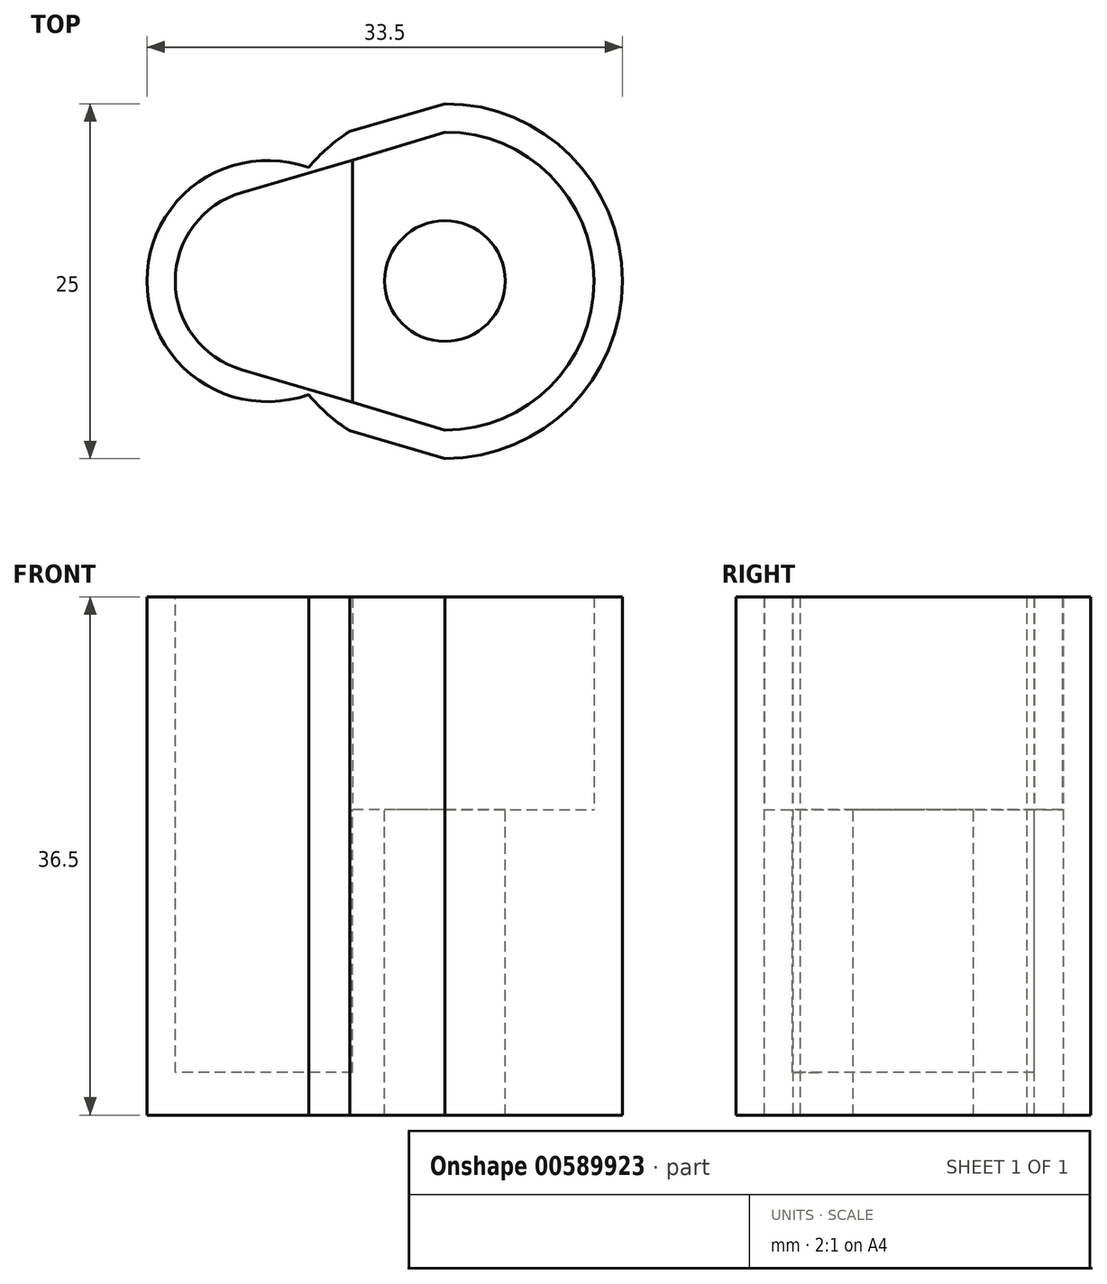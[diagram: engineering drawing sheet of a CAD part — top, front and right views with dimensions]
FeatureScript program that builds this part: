
annotation { "Feature Type Name" : "Feature", "Feature Type Description" : "" }
export const myFeature = defineFeature(function(context is Context, id is Id, definition is map)
    precondition{}
    {
        {
            var Q0;
            Q0=qCreatedBy(makeId("Top.planeOp"),FACE);
            var sketch = newSketch(context, id + "F0", { "sketchPlane" : qUnion([Q0])});
            skCircle(sketch, "E0", {"center": v(0, 0) * mm, "radius": 4 * mm});
            skCircle(sketch, "E1", {"center": v(0, 0) * mm, "radius": 12.5 * mm});
            skCircle(sketch, "E2", {"center": v(-12.5, 0) * mm, "radius": 8.5 * mm});
            skLineSegment(sketch, "E3", {"start": v(0, -12.5) * mm, "end": v(-14.88, -8.16) * mm});
            skLineSegment(sketch, "E4", {"start": v(0, 12.5) * mm, "end": v(-14.88, 8.16) * mm});
            skSolve(sketch);
        }
        {
            var Q0;
            {var subQ10=sQuery(id+"F0.wireOp",EDGE,"E0");Q0=makeQuery(id+"F0.imprint","IMPRINT",FACE,{"disambiguationData":[TD([[makeQuery(id+"F0.imprint","IMPRINT",EDGE,{"derivedFrom":subQ10}),-1.0]])]});}
            var Q1;
            {var subQ0=sQuery(id+"F0.wireOp",EDGE,"E3");var subQ1=sQuery(id+"F0.wireOp",EDGE,"E1");var subQ2=makeQuery(id+"F0.imprint","INTERSECT",VERTEX,{"disambiguationData":[OD(1.0)],"derivedFrom":[subQ1,subQ0]});Q1=makeQuery(id+"F0.imprint","IMPRINT",FACE,{"disambiguationData":[TD([[makeQuery(id+"F0.imprint","IMPRINT",EDGE,{"disambiguationData":[TD([[subQ2,1.0]])],"derivedFrom":subQ1}),-1.0]])]});}
            var Q2;
            {var subQ0=sQuery(id+"F0.wireOp",EDGE,"E2");var subQ1=sQuery(id+"F0.wireOp",EDGE,"E1");var subQ2=makeQuery(id+"F0.imprint","INTERSECT",VERTEX,{"disambiguationData":[OD(0.0)],"derivedFrom":[subQ1,subQ0]});Q2=makeQuery(id+"F0.imprint","IMPRINT",FACE,{"disambiguationData":[TD([[makeQuery(id+"F0.imprint","IMPRINT",EDGE,{"disambiguationData":[TD([[subQ2,-1.0]])],"derivedFrom":subQ1}),-1.0]])]});}
            var Q3;
            {var subQ0=sQuery(id+"F0.wireOp",EDGE,"E2");var subQ1=sQuery(id+"F0.wireOp",EDGE,"E1");var subQ2=makeQuery(id+"F0.imprint","INTERSECT",VERTEX,{"disambiguationData":[OD(0.0)],"derivedFrom":[subQ1,subQ0]});Q3=makeQuery(id+"F0.imprint","IMPRINT",FACE,{"disambiguationData":[TD([[makeQuery(id+"F0.imprint","IMPRINT",EDGE,{"disambiguationData":[TD([[subQ2,-1.0]])],"derivedFrom":subQ1}),1.0]])]});}
            var Q4;
            {var subQ0=sQuery(id+"F0.wireOp",EDGE,"E4");var subQ1=sQuery(id+"F0.wireOp",EDGE,"E1");var subQ2=makeQuery(id+"F0.imprint","INTERSECT",VERTEX,{"disambiguationData":[OD(1.0)],"derivedFrom":[subQ1,subQ0]});Q4=makeQuery(id+"F0.imprint","IMPRINT",FACE,{"disambiguationData":[TD([[makeQuery(id+"F0.imprint","IMPRINT",EDGE,{"disambiguationData":[TD([[subQ2,-1.0]])],"derivedFrom":subQ1}),-1.0]])]});}
            extrude(context, id + "F1", {"entities" : qUnion([Q0, Q1, Q2, Q3, Q4]), "depth" : 30 * mm, "offsetDistance" : 25 * mm});
        }
        {
            var Q0;
            Q0=makeQuery(id+"F1.opExtrude","CAP_FACE",FACE,{"disambiguationData":[OSD([sQuery(id+"F0.wireOp",EDGE,"E0"),sQuery(id+"F0.wireOp",EDGE,"E1"),sQuery(id+"F0.wireOp",EDGE,"E2"),sQuery(id+"F0.wireOp",EDGE,"E3"),sQuery(id+"F0.wireOp",EDGE,"E4")])],"isStart":false});
            var sketch = newSketch(context, id + "F2", { "sketchPlane" : qUnion([Q0])});
            skLineSegment(sketch, "E5.0", {"start": v(0.56, -10.58) * mm, "end": v(-14.32, -6.24) * mm});
            skArc(sketch, "E5.1", {"start": v(-14.32, 6.24) * mm, "mid": v(-19, 0) * mm, "end": v(-14.32, -6.24) * mm});
            skLineSegment(sketch, "E5.2", {"start": v(0.56, 10.58) * mm, "end": v(-14.32, 6.24) * mm});
            skLineSegment(sketch, "E6.bottom", {"start": v(6.5, 6.5) * mm, "end": v(-6.5, 6.5) * mm});
            skLineSegment(sketch, "E6.top", {"start": v(6.5, -6.5) * mm, "end": v(-6.5, -6.5) * mm});
            skLineSegment(sketch, "E6.right", {"start": v(-6.5, 6.5) * mm, "end": v(-6.5, -6.5) * mm});
            skPoint(sketch, "E6.middle", {"position": v(0, 0) * mm});
            skLineSegment(sketch, "E7", {"start": v(-6.5, -6.5) * mm, "end": v(-6.5, -8.52) * mm});
            skLineSegment(sketch, "E8", {"start": v(-6.5, 6.5) * mm, "end": v(-6.5, 8.52) * mm});
            skLineSegment(sketch, "E9", {"start": v(6.5, 0) * mm, "end": v(10, 0) * mm, "construction": true});
            skPoint(sketch, "E9.endSnap0", {"position": v(6.5, 0) * mm});
            skLineSegment(sketch, "E10", {"start": v(10, 0) * mm, "end": v(6.5, 6.5) * mm});
            skLineSegment(sketch, "E11", {"start": v(10, 0) * mm, "end": v(6.5, -6.5) * mm});
            skSolve(sketch);
        }
        {
            var Q0;
            {var subQ1=sQuery(id+"F2.wireOp",EDGE,"E5.1");Q0=makeQuery(id+"F2.imprint","IMPRINT",FACE,{"disambiguationData":[TD([[makeQuery(id+"F2.imprint","IMPRINT",EDGE,{"derivedFrom":subQ1}),1.0]])]});}
            extrude(context, id + "F3", {"entities" : qUnion([Q0]), "operationType" : NewBodyOperationType.REMOVE, "oppositeDirection" : true, "depth" : 27 * mm, "offsetDistance" : 25 * mm});
        }
        {
            var Q0;
            Q0=makeQuery(id+"F1.opExtrude","CAP_FACE",FACE,{"disambiguationData":[OSD([sQuery(id+"F0.wireOp",EDGE,"E0"),sQuery(id+"F0.wireOp",EDGE,"E1"),sQuery(id+"F0.wireOp",EDGE,"E2"),sQuery(id+"F0.wireOp",EDGE,"E3"),sQuery(id+"F0.wireOp",EDGE,"E4")])],"isStart":false});
            var sketch = newSketch(context, id + "F4", { "sketchPlane" : qUnion([Q0])});
            skCircle(sketch, "E12", {"center": v(0, 0) * mm, "radius": 4.25 * mm});
            skSolve(sketch);
        }
        {
            var Q0;
            Q0=makeQuery(id+"F2.imprint","IMPRINT",FACE,{"disambiguationData":[TD([[makeQuery(id+"F2.imprint","IMPRINT",EDGE,{"derivedFrom":sQuery(id+"F2.wireOp",EDGE,"E6.bottom")}),1.0]])]});
            extrude(context, id + "F5", {"entities" : qUnion([Q0]), "operationType" : NewBodyOperationType.REMOVE, "oppositeDirection" : true, "depth" : 6.5 * mm, "offsetDistance" : 25 * mm});
        }
        {
            var Q0;
            Q0=makeQuery(id+"F4.imprint","IMPRINT",FACE,{"disambiguationData":[TD([[makeQuery(id+"F4.imprint","IMPRINT",EDGE,{"derivedFrom":sQuery(id+"F4.wireOp",EDGE,"E12")}),1.0]])]});
            extrude(context, id + "F6", {"entities" : qUnion([Q0]), "operationType" : NewBodyOperationType.REMOVE, "oppositeDirection" : true, "depth" : 35.2 * mm, "offsetDistance" : 25 * mm});
        }
        {
            var Q0;
            Q0=makeQuery(id+"F1.opExtrude","CAP_FACE",FACE,{"disambiguationData":[OSD([sQuery(id+"F0.wireOp",EDGE,"E0"),sQuery(id+"F0.wireOp",EDGE,"E1"),sQuery(id+"F0.wireOp",EDGE,"E2"),sQuery(id+"F0.wireOp",EDGE,"E3"),sQuery(id+"F0.wireOp",EDGE,"E4")])],"isStart":false});
            extrude(context, id + "F7", {"entities" : qUnion([Q0]), "operationType" : NewBodyOperationType.ADD, "depth" : 10 * mm, "offsetDistance" : 25 * mm});
        }
        {
            var Q0;
            {var subQ0=sQuery(id+"F2.wireOp",EDGE,"E6.bottom");Q0=makeQuery(id+"F7.boolean.opBoolean","MERGE",FACE,{"derivedFrom":[makeQuery(id+"F5.boolean.opBoolean","COPY",FACE,{"derivedFrom":makeQuery(id+"F5.opExtrude","SWEPT_FACE",FACE,{"disambiguationData":[OSD([subQ0])]})}),makeQuery(id+"F7.opExtrude","SWEPT_FACE",FACE,{"disambiguationData":[OSD([subQ0])]})]});}
            var sketch = newSketch(context, id + "F8", { "sketchPlane" : qUnion([Q0])});
            skLineSegment(sketch, "E13.0", {"start": v(-5.5, 23.5) * mm, "end": v(-5.5, 40) * mm});
            skSolve(sketch);
        }
        {
            var Q0;
            {var subQ0=sQuery(id+"F8.wireOp",EDGE,"E13.0");Q0=makeQuery(id+"F8.imprint","IMPRINT",FACE,{"disambiguationData":[TD([[makeQuery(id+"F8.imprint","IMPRINT",EDGE,{"derivedFrom":subQ0}),1.0]])]});}
            extrude(context, id + "F9", {"entities" : qUnion([Q0]), "operationType" : NewBodyOperationType.ADD, "depth" : 13.4 * mm, "offsetDistance" : 25 * mm});
        }
        {
            var Q0;
            {var subQ2=sQuery(id+"F2.wireOp",EDGE,"E6.bottom");var subQ3=makeQuery(id+"F7.opExtrude","CAP_EDGE",EDGE,{"disambiguationData":[OSD([subQ2])],"isStart":false});Q0=makeQuery(id+"F9.boolean.opBoolean","MERGE",FACE,{"derivedFrom":[makeQuery(id+"F7.opExtrude","CAP_FACE",FACE,{"disambiguationData":[OSD([sQuery(id+"F0.wireOp",EDGE,"E0"),sQuery(id+"F0.wireOp",EDGE,"E1"),sQuery(id+"F0.wireOp",EDGE,"E2"),sQuery(id+"F0.wireOp",EDGE,"E3"),sQuery(id+"F0.wireOp",EDGE,"E4")])],"isStart":false}),makeQuery(id+"F9.opExtrude","SWEPT_FACE",FACE,{"disambiguationData":[OSD([subQ2]),TDD([makeQuery(id+"F8.imprint","IMPRINT",EDGE,{"disambiguationData":[TD([[makeQuery(id+"F8.imprint","INTERSECT",VERTEX,{"derivedFrom":[subQ3,sQuery(id+"F8.wireOp",EDGE,"E13.0")]}),-1.0]])],"derivedFrom":subQ3})])]})]});}
            var sketch = newSketch(context, id + "F10", { "sketchPlane" : qUnion([Q0])});
            skLineSegment(sketch, "E14", {"start": v(-5.5, -6.5) * mm, "end": v(0, -12.5) * mm});
            skLineSegment(sketch, "E15", {"start": v(-5.5, 6.5) * mm, "end": v(0, 12.5) * mm});
            skSolve(sketch);
        }
        {
            var Q0;
            Q0=makeQuery(id+"F10.imprint","IMPRINT",FACE,{"disambiguationData":[TD([[makeQuery(id+"F10.imprint","IMPRINT",EDGE,{"derivedFrom":sQuery(id+"F10.wireOp",EDGE,"E14")}),1.0]])]});
            extrude(context, id + "F11", {"entities" : qUnion([Q0]), "operationType" : NewBodyOperationType.REMOVE, "oppositeDirection" : true, "depth" : 16 * mm, "offsetDistance" : 25 * mm});
        }
        {
            var Q0;
            Q0=makeQuery(id+"F11.boolean.opBoolean","COPY",FACE,{"derivedFrom":makeQuery(id+"F11.opExtrude","CAP_FACE",FACE,{"disambiguationData":[OSD([sQuery(id+"F0.wireOp",EDGE,"E1"),sQuery(id+"F2.wireOp",EDGE,"E6.bottom"),sQuery(id+"F2.wireOp",EDGE,"E6.top"),sQuery(id+"F2.wireOp",EDGE,"E10"),sQuery(id+"F2.wireOp",EDGE,"E11"),sQuery(id+"F10.wireOp",EDGE,"E14"),sQuery(id+"F10.wireOp",EDGE,"E15")])],"isStart":false})});
            extrude(context, id + "F12", {"entities" : qUnion([Q0]), "operationType" : NewBodyOperationType.REMOVE, "oppositeDirection" : true, "depth" : .5 * mm, "offsetDistance" : 25 * mm});
        }
        {
            var Q0;
            Q0=makeQuery(id+"F9.opExtrude","SWEPT_FACE",FACE,{"disambiguationData":[OSD([sQuery(id+"F8.wireOp",EDGE,"E13.0")])]});
            var sketch = newSketch(context, id + "F13", { "sketchPlane" : qUnion([Q0])});
            skCircle(sketch, "E16", {"center": v(0, 31.75) * mm, "radius": 1.25 * mm});
            skPoint(sketch, "E16.centerSnap0", {"position": v(-6.5, 31.75) * mm});
            skPoint(sketch, "E16.centerSnap1", {"position": v(0, 40) * mm});
            skSolve(sketch);
        }
        {
            var Q0;
            Q0=makeQuery(id+"F13.imprint","IMPRINT",FACE,{"disambiguationData":[TD([[makeQuery(id+"F13.imprint","IMPRINT",EDGE,{"derivedFrom":sQuery(id+"F13.wireOp",EDGE,"E16")}),1.0]])]});
            extrude(context, id + "F14", {"entities" : qUnion([Q0]), "operationType" : NewBodyOperationType.REMOVE, "oppositeDirection" : true, "depth" : 25 * mm, "offsetDistance" : 25 * mm});
        }
        {
            var Q0;
            {var subQ0=sQuery(id+"F2.wireOp",EDGE,"E11");var subQ1=sQuery(id+"F2.wireOp",EDGE,"E10");var subQ2=sQuery(id+"F2.wireOp",EDGE,"E6.top");var subQ3=sQuery(id+"F2.wireOp",EDGE,"E6.bottom");Q0=makeQuery(id+"F12.boolean.opBoolean","MERGE",FACE,{"derivedFrom":[makeQuery(id+"F5.boolean.opBoolean","COPY",FACE,{"derivedFrom":makeQuery(id+"F5.opExtrude","CAP_FACE",FACE,{"disambiguationData":[OSD([sQuery(id+"F0.wireOp",EDGE,"E0"),subQ3,subQ2,sQuery(id+"F2.wireOp",EDGE,"E6.right"),subQ1,subQ0])],"isStart":false})})],"fromTools":[makeQuery(id+"F12.opExtrude","CAP_FACE",FACE,{"disambiguationData":[OSD([sQuery(id+"F0.wireOp",EDGE,"E1"),subQ3,subQ2,subQ1,subQ0,sQuery(id+"F10.wireOp",EDGE,"E14"),sQuery(id+"F10.wireOp",EDGE,"E15")])],"isStart":false})]});}
            extrude(context, id + "F15", {"entities" : qUnion([Q0]), "operationType" : NewBodyOperationType.REMOVE, "oppositeDirection" : true, "depth" : 2 * mm, "offsetDistance" : 25 * mm});
        }
        {
            var Q0;
            {var subQ2=sQuery(id+"F2.wireOp",EDGE,"E6.bottom");var subQ3=makeQuery(id+"F7.opExtrude","CAP_EDGE",EDGE,{"disambiguationData":[OSD([subQ2])],"isStart":false});Q0=makeQuery(id+"F9.boolean.opBoolean","MERGE",FACE,{"derivedFrom":[makeQuery(id+"F7.opExtrude","CAP_FACE",FACE,{"disambiguationData":[OSD([sQuery(id+"F0.wireOp",EDGE,"E0"),sQuery(id+"F0.wireOp",EDGE,"E1"),sQuery(id+"F0.wireOp",EDGE,"E2"),sQuery(id+"F0.wireOp",EDGE,"E3"),sQuery(id+"F0.wireOp",EDGE,"E4")])],"isStart":false}),makeQuery(id+"F9.opExtrude","SWEPT_FACE",FACE,{"disambiguationData":[OSD([subQ2]),TDD([makeQuery(id+"F8.imprint","IMPRINT",EDGE,{"disambiguationData":[TD([[makeQuery(id+"F8.imprint","INTERSECT",VERTEX,{"derivedFrom":[subQ3,sQuery(id+"F8.wireOp",EDGE,"E13.0")]}),-1.0]])],"derivedFrom":subQ3})])]})]});}
            extrude(context, id + "F16", {"entities" : qUnion([Q0]), "operationType" : NewBodyOperationType.REMOVE, "oppositeDirection" : true, "depth" : 18.5 * mm, "offsetDistance" : 25 * mm});
        }
        {
            var Q0;
            {var subQ0=sQuery(id+"F2.wireOp",EDGE,"E6.bottom");var subQ1=sQuery(id+"F0.wireOp",EDGE,"E1");var subQ2=sQuery(id+"F0.wireOp",EDGE,"E0");Q0=makeQuery(id+"F16.boolean.opBoolean","MERGE",FACE,{"derivedFrom":[makeQuery(id+"F15.boolean.opBoolean","COPY",FACE,{"derivedFrom":makeQuery(id+"F15.opExtrude","CAP_FACE",FACE,{"disambiguationData":[OSD([subQ2,subQ1,subQ0,sQuery(id+"F2.wireOp",EDGE,"E6.top"),sQuery(id+"F2.wireOp",EDGE,"E6.right"),sQuery(id+"F2.wireOp",EDGE,"E10"),sQuery(id+"F2.wireOp",EDGE,"E11"),sQuery(id+"F10.wireOp",EDGE,"E14"),sQuery(id+"F10.wireOp",EDGE,"E15")])],"isStart":false})})],"fromTools":[makeQuery(id+"F16.opExtrude","CAP_FACE",FACE,{"disambiguationData":[OSD([subQ2,subQ1,sQuery(id+"F0.wireOp",EDGE,"E2"),sQuery(id+"F0.wireOp",EDGE,"E3"),sQuery(id+"F0.wireOp",EDGE,"E4"),subQ0])],"isStart":false})]});}
            var sketch = newSketch(context, id + "F17", { "sketchPlane" : qUnion([Q0])});
            skArc(sketch, "E17.0", {"start": v(0, -10.5) * mm, "mid": v(10.5, 0) * mm, "end": v(0, 10.5) * mm});
            skLineSegment(sketch, "E18", {"start": v(0, 10.5) * mm, "end": v(-6.5, 8.52) * mm});
            skLineSegment(sketch, "E19", {"start": v(0, -10.5) * mm, "end": v(-6.5, -8.52) * mm});
            skSolve(sketch);
        }
        {
            var Q0;
            Q0=makeQuery(id+"F17.imprint","IMPRINT",FACE,{"disambiguationData":[TD([[makeQuery(id+"F17.imprint","IMPRINT",EDGE,{"derivedFrom":sQuery(id+"F17.wireOp",EDGE,"E17.0")}),-1.0]])]});
            extrude(context, id + "F18", {"entities" : qUnion([Q0]), "operationType" : NewBodyOperationType.ADD, "depth" : 15 * mm, "offsetDistance" : 25 * mm});
        }
    });
